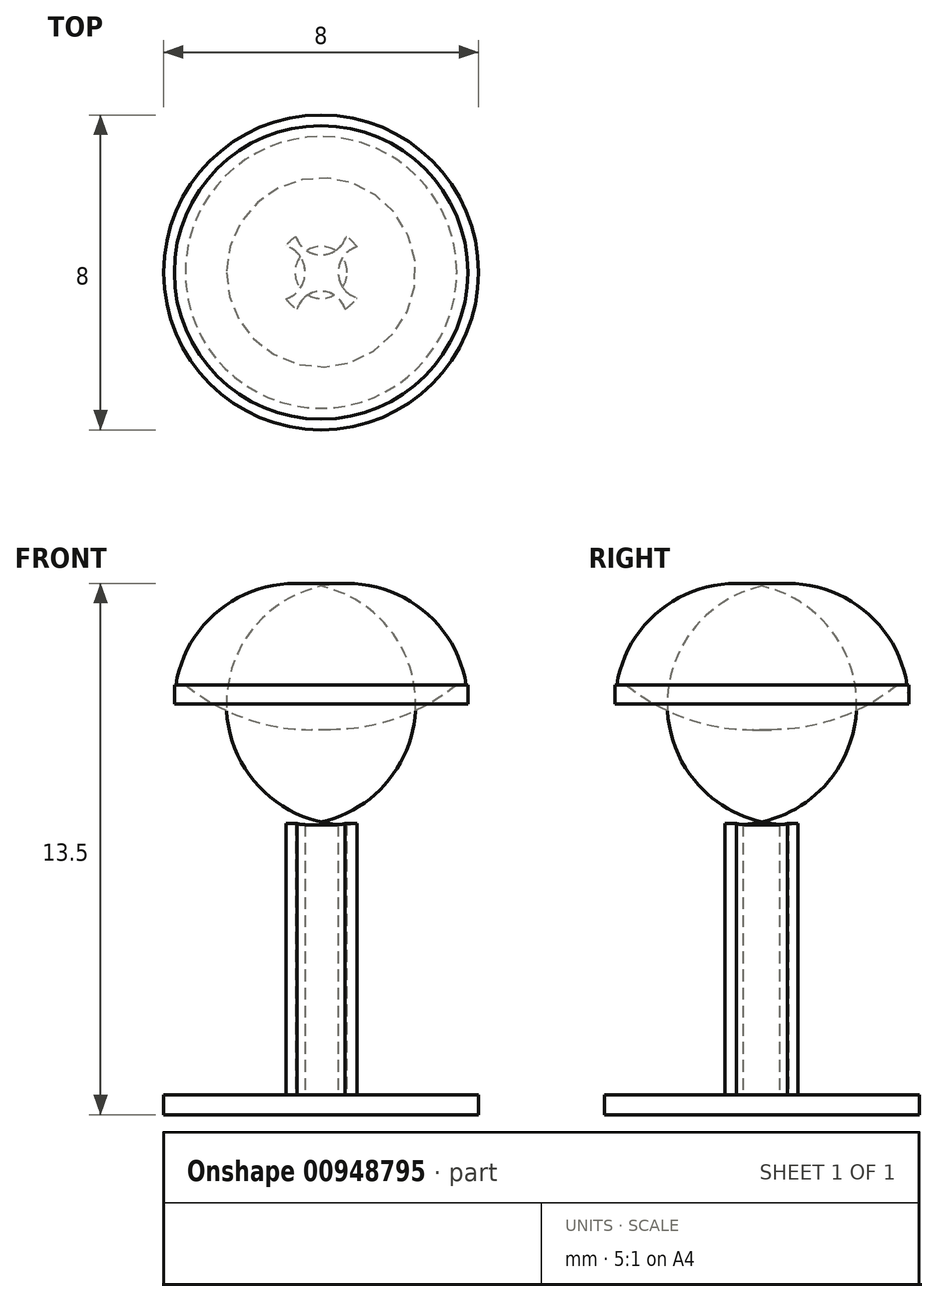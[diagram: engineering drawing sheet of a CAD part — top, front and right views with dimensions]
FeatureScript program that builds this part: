
annotation { "Feature Type Name" : "Feature", "Feature Type Description" : "" }
export const myFeature = defineFeature(function(context is Context, id is Id, definition is map)
    precondition{}
    {
        {
            var Q0;
            Q0=qCreatedBy(makeId("Top.planeOp"),FACE);
            var sketch = newSketch(context, id + "F0", { "sketchPlane" : qUnion([Q0])});
            skCircle(sketch, "E0", {"center": v(0, 0) * mm, "radius": 4 * mm});
            skSolve(sketch);
        }
        {
            var Q0;
            Q0 = qSketchRegion(id + "F0", true);
            extrude(context, id + "F1", {"entities" : qUnion([Q0]), "depth" : 0.5 * mm, "offsetDistance" : 25.4 * mm});
        }
        {
            var Q0;
            Q0=makeQuery(id+"F1.opExtrude","CAP_FACE",FACE,{"disambiguationData":[OSD([sQuery(id+"F0.wireOp",EDGE,"E0")])],"isStart":false});
            var sketch = newSketch(context, id + "F2", { "sketchPlane" : qUnion([Q0])});
            skCircle(sketch, "E1", {"center": v(0, 0) * mm, "radius": 1.12 * mm});
            skCircle(sketch, "E2", {"center": v(0, -1.12) * mm, "radius": 0.64 * mm});
            skCircle(sketch, "E3", {"center": v(1.12, 0) * mm, "radius": 0.68 * mm});
            skCircle(sketch, "E4", {"center": v(0, 1.12) * mm, "radius": 0.67 * mm});
            skCircle(sketch, "E5", {"center": v(-1.12, 0) * mm, "radius": 0.71 * mm});
            skSolve(sketch);
        }
        {
            var Q0;
            {var subQ1=sQuery(id+"F2.wireOp",EDGE,"E1");var subQ9=sQuery(id+"F2.wireOp",EDGE,"E4");var subQ11=makeQuery(id+"F2.imprint","INTERSECT",VERTEX,{"disambiguationData":[OD(0.0)],"derivedFrom":[subQ1,subQ9]});Q0=makeQuery(id+"F2.imprint","IMPRINT",FACE,{"disambiguationData":[TD([[makeQuery(id+"F2.imprint","IMPRINT",EDGE,{"disambiguationData":[TD([[subQ11,1.0]])],"derivedFrom":subQ1}),1.0]])]});}
            extrude(context, id + "F3", {"entities" : qUnion([Q0]), "operationType" : NewBodyOperationType.ADD, "depth" : 6.86 * mm, "offsetDistance" : 25.4 * mm});
        }
        {
            var Q0;
            Q0=makeQuery(id+"F3.opExtrude","CAP_FACE",FACE,{"disambiguationData":[OSD([sQuery(id+"F2.wireOp",EDGE,"E1"),sQuery(id+"F2.wireOp",EDGE,"E2"),sQuery(id+"F2.wireOp",EDGE,"E3"),sQuery(id+"F2.wireOp",EDGE,"E4"),sQuery(id+"F2.wireOp",EDGE,"E5")])],"isStart":false});
            var sketch = newSketch(context, id + "F4", { "sketchPlane" : qUnion([Q0])});
            skCircle(sketch, "E6", {"center": v(0, 0) * mm, "radius": 3.73 * mm});
            skSolve(sketch);
        }
        {
            var Q0;
            Q0 = qSketchRegion(id + "F4", true);
            extrude(context, id + "F5", {"entities" : qUnion([Q0]), "operationType" : NewBodyOperationType.ADD, "depth" : 3.56 * mm, "offsetDistance" : 25.4 * mm});
        }
        {
            var Q0;
            Q0=makeQuery(id+"F5.opExtrude","CAP_EDGE",EDGE,{"disambiguationData":[OSD([sQuery(id+"F4.wireOp",EDGE,"E6")])],"isStart":true});
            fillet(context, id + "F6", {"entities" : qUnion([Q0]), "radius" : 3.07 * mm, "tangentPropagation" : true, "allowEdgeOverflow" : false});
        }
        {
            var Q0;
            Q0=makeQuery(id+"F5.opExtrude","CAP_FACE",FACE,{"disambiguationData":[OSD([sQuery(id+"F4.wireOp",EDGE,"E6")])],"isStart":false});
            var sketch = newSketch(context, id + "F7", { "sketchPlane" : qUnion([Q0])});
            skCircle(sketch, "E7.0", {"center": v(0, 0) * mm, "radius": 3.45 * mm});
            skSolve(sketch);
        }
        {
            var Q0;
            Q0=makeQuery(id+"F7.imprint","IMPRINT",FACE,{"disambiguationData":[TD([[makeQuery(id+"F7.imprint","IMPRINT",EDGE,{"derivedFrom":sQuery(id+"F7.wireOp",EDGE,"E7.0")}),1.0]])]});
            extrude(context, id + "F8", {"entities" : qUnion([Q0]), "operationType" : NewBodyOperationType.REMOVE, "oppositeDirection" : true, "depth" : 1.14 * mm, "offsetDistance" : 25.4 * mm});
        }
        {
            var Q0;
            Q0=makeQuery(id+"F8.boolean.opBoolean","COPY",EDGE,{"derivedFrom":makeQuery(id+"F8.opExtrude","CAP_EDGE",EDGE,{"disambiguationData":[OSD([sQuery(id+"F7.wireOp",EDGE,"E7.0")])],"isStart":false})});
            fillet(context, id + "F9", {"entities" : qUnion([Q0]), "radius" : 5.08 * mm, "tangentPropagation" : true, "allowEdgeOverflow" : false});
        }
    });
